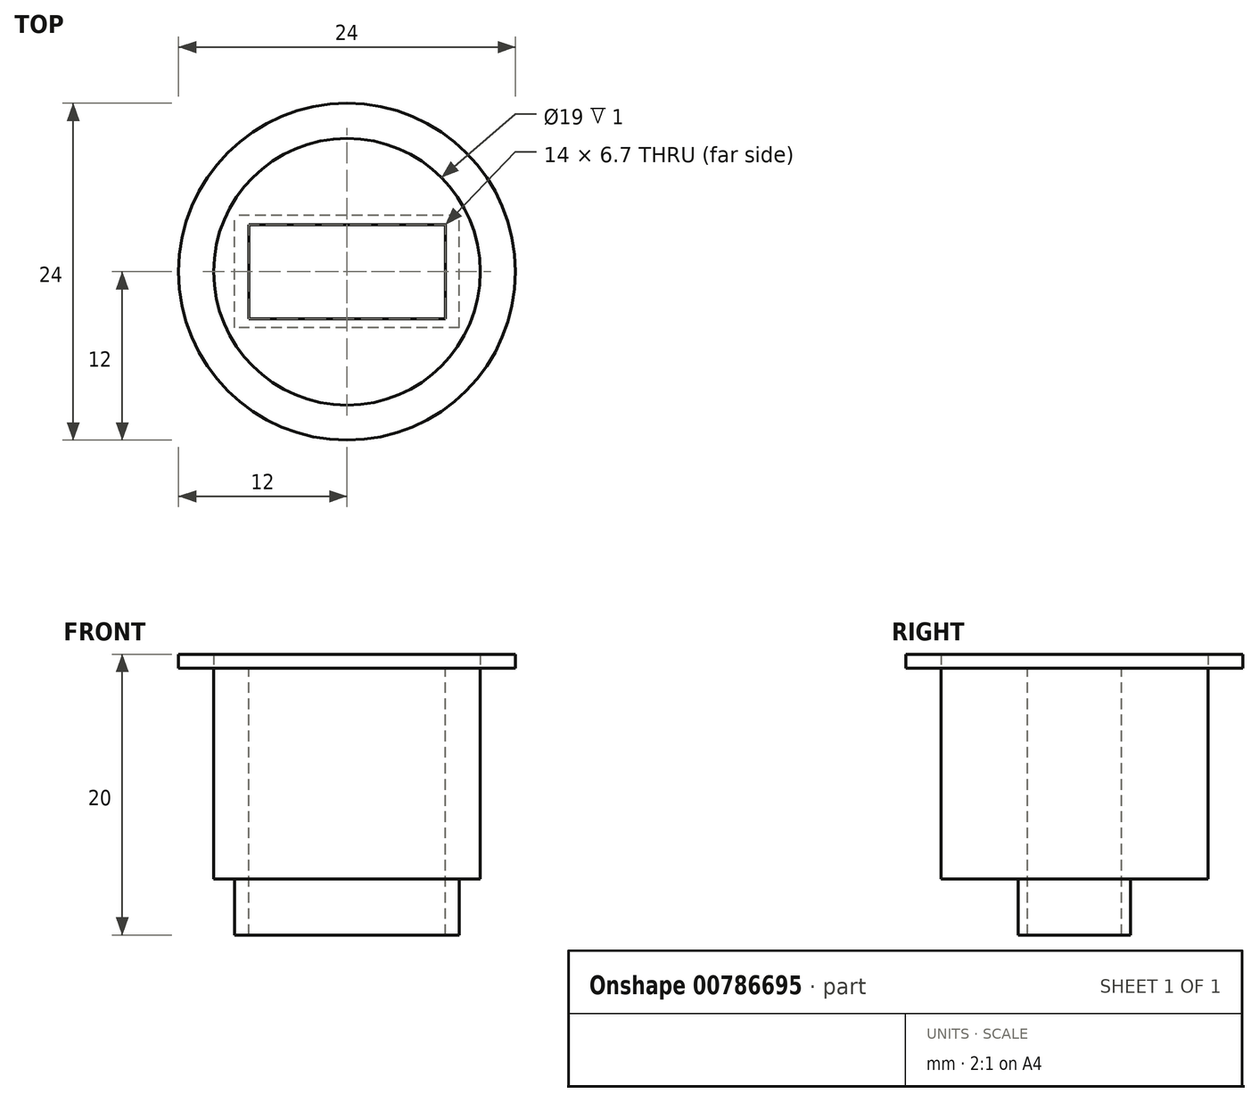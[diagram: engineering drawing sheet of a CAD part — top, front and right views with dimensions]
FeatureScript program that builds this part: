
annotation { "Feature Type Name" : "Feature", "Feature Type Description" : "" }
export const myFeature = defineFeature(function(context is Context, id is Id, definition is map)
    precondition{}
    {
        {
            var Q0;
            Q0=qCreatedBy(makeId("Top.planeOp"),FACE);
            var sketch = newSketch(context, id + "F0", { "sketchPlane" : qUnion([Q0])});
            skLineSegment(sketch, "E0.bottom", {"start": v(-7, 3.35) * mm, "end": v(7, 3.35) * mm});
            skLineSegment(sketch, "E0.top", {"start": v(-7, -3.35) * mm, "end": v(7, -3.35) * mm});
            skLineSegment(sketch, "E0.left", {"start": v(-7, 3.35) * mm, "end": v(-7, -3.35) * mm});
            skLineSegment(sketch, "E0.right", {"start": v(7, 3.35) * mm, "end": v(7, -3.35) * mm});
            skCircle(sketch, "E1", {"center": v(0, 0) * mm, "radius": 9.5 * mm});
            skCircle(sketch, "E2", {"center": v(0, 0) * mm, "radius": 12 * mm});
            skLineSegment(sketch, "E3.bottom", {"start": v(8, -4) * mm, "end": v(-8, -4) * mm});
            skLineSegment(sketch, "E3.top", {"start": v(8, 4) * mm, "end": v(-8, 4) * mm});
            skLineSegment(sketch, "E3.left", {"start": v(8, -4) * mm, "end": v(8, 4) * mm});
            skLineSegment(sketch, "E3.right", {"start": v(-8, -4) * mm, "end": v(-8, 4) * mm});
            skSolve(sketch);
        }
        {
            var Q0;
            Q0=makeQuery(id+"F0.imprint","IMPRINT",FACE,{"disambiguationData":[TD([[makeQuery(id+"F0.imprint","IMPRINT",EDGE,{"derivedFrom":sQuery(id+"F0.wireOp",EDGE,"E0.bottom")}),1.0]])]});
            extrude(context, id + "F1", {"entities" : qUnion([Q0]), "depth" : -19 * mm, "offsetDistance" : 25 * mm});
        }
        {
            var Q0;
            Q0 = qSketchRegion(id + "F0", true);
            extrude(context, id + "F2", {"entities" : qUnion([Q0]), "depth" : 1 * mm, "offsetDistance" : 25 * mm});
        }
        {
            var Q0;
            Q0=makeQuery(id+"F0.imprint","IMPRINT",FACE,{"disambiguationData":[TD([[makeQuery(id+"F0.imprint","IMPRINT",EDGE,{"derivedFrom":sQuery(id+"F0.wireOp",EDGE,"E1")}),1.0]])]});
            extrude(context, id + "F3", {"entities" : qUnion([Q0]), "operationType" : NewBodyOperationType.ADD, "depth" : -15 * mm, "offsetDistance" : 25 * mm});
        }
    });
